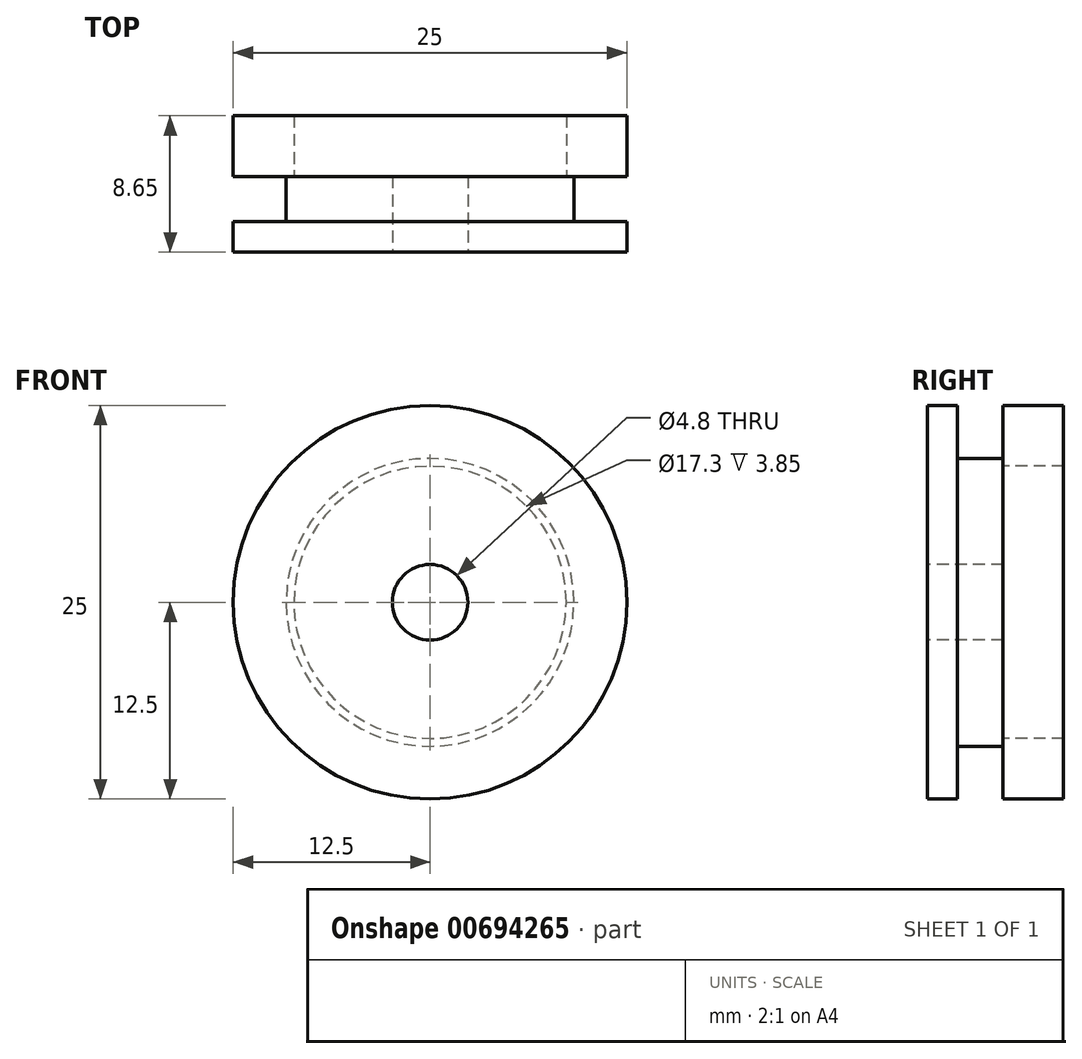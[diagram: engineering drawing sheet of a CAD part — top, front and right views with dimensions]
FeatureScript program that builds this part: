
annotation { "Feature Type Name" : "Feature", "Feature Type Description" : "" }
export const myFeature = defineFeature(function(context is Context, id is Id, definition is map)
    precondition{}
    {
        {
            var Q0;
            Q0=qCreatedBy(makeId("Right.planeOp"),FACE);
            var sketch = newSketch(context, id + "F0", { "sketchPlane" : qUnion([Q0])});
            skLineSegment(sketch, "E0", {"start": v(0, 0) * mm, "end": v(0, 12.5) * mm});
            skLineSegment(sketch, "E1", {"start": v(0, 12.5) * mm, "end": v(1.92, 12.5) * mm});
            skLineSegment(sketch, "E2", {"start": v(1.92, 12.5) * mm, "end": v(1.92, 9.14) * mm});
            skLineSegment(sketch, "E3", {"start": v(1.92, 9.14) * mm, "end": v(4.8, 9.14) * mm});
            skLineSegment(sketch, "E4", {"start": v(4.8, 9.14) * mm, "end": v(4.8, 12.5) * mm});
            skLineSegment(sketch, "E5", {"start": v(4.8, 12.5) * mm, "end": v(8.65, 12.5) * mm});
            skPoint(sketch, "E6.end.orphan", {"position": v(0, 2.4) * mm});
            skLineSegment(sketch, "E7", {"start": v(8.65, 12.5) * mm, "end": v(8.65, 8.65) * mm});
            skLineSegment(sketch, "E8", {"start": v(8.65, 8.65) * mm, "end": v(4.8, 8.65) * mm});
            skLineSegment(sketch, "E9", {"start": v(4.8, 8.65) * mm, "end": v(4.8, 2.4) * mm});
            skLineSegment(sketch, "E10", {"start": v(4.8, 2.4) * mm, "end": v(0, 2.4) * mm});
            skLineSegment(sketch, "E11", {"start": v(0, 0) * mm, "end": v(39.3, 0) * mm, "construction": true});
            skSolve(sketch);
        }
        {
            var Q0;
            Q0=qSketchRegion(id+"F0",true);
            var Q1;
            Q1=sQuery(id+"F0.wireOp",EDGE,"E11");
            revolve(context, id + "F1", {"entities" : qUnion([Q0]), "axis" : qUnion([Q1]), "revolveType" : RevolveType.FULL});
        }
    });
